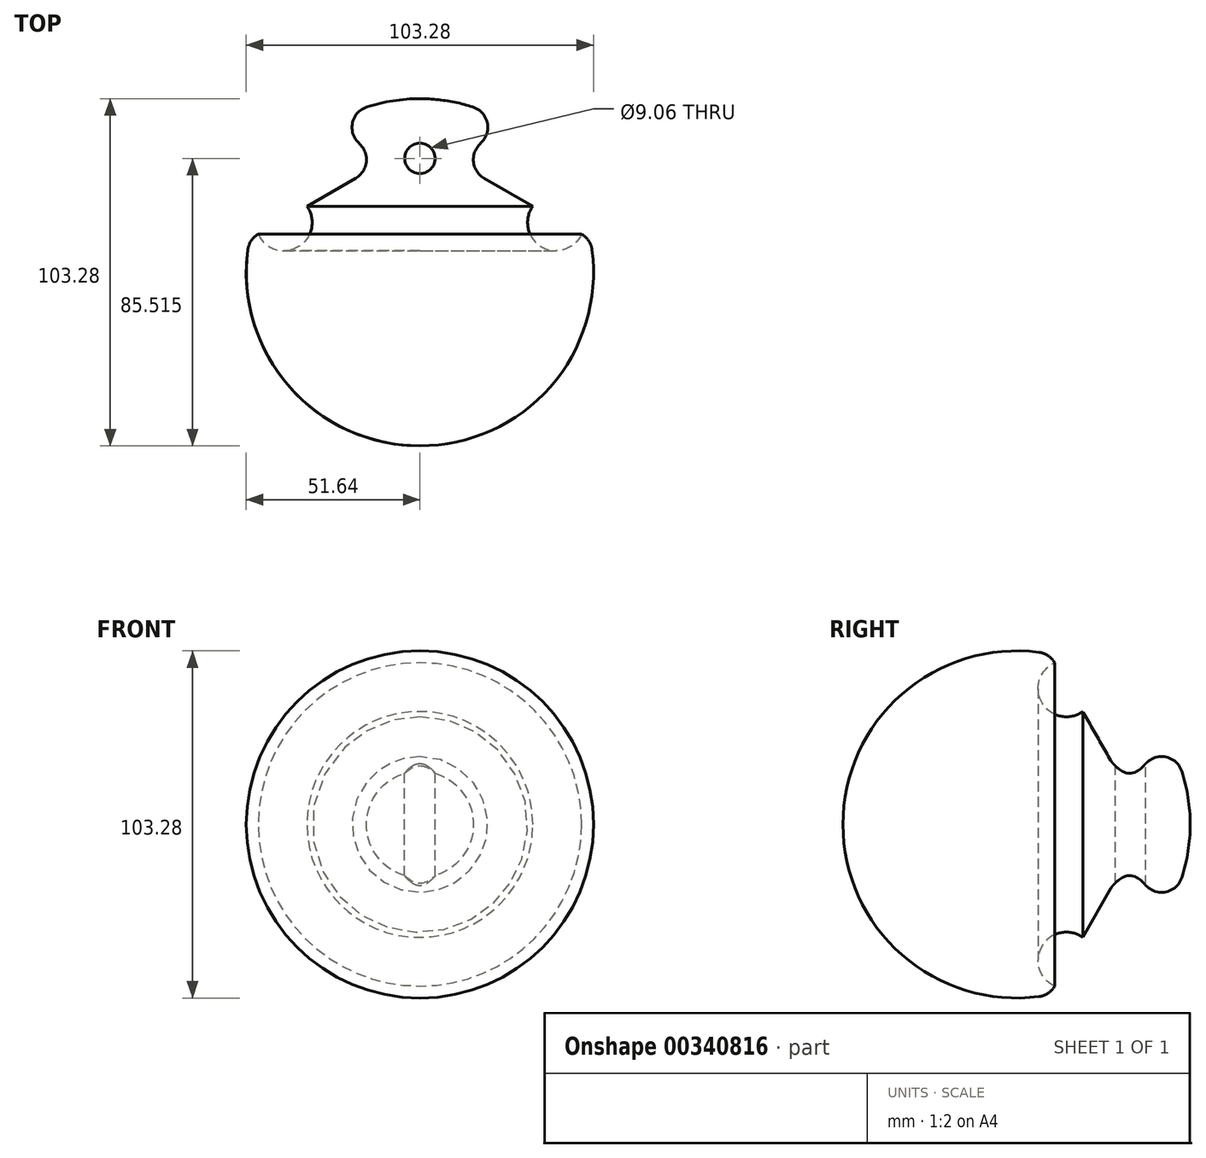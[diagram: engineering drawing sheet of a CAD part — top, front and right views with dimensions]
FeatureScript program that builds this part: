
annotation { "Feature Type Name" : "Feature", "Feature Type Description" : "" }
export const myFeature = defineFeature(function(context is Context, id is Id, definition is map)
    precondition{}
    {
        {
            var Q0;
            Q0=qCreatedBy(makeId("Top.planeOp"),FACE);
            var sketch = newSketch(context, id + "F0", { "sketchPlane" : qUnion([Q0])});
            skArc(sketch, "E0", {"start": v(0, 51.64) * mm, "mid": v(-7.98, 51.02) * mm, "end": v(-15.77, 49.18) * mm});
            skLineSegment(sketch, "E1", {"start": v(0, 51.64) * mm, "end": v(0, -51.64) * mm});
            skLineSegment(sketch, "E2", {"start": v(-18.54, 38.86) * mm, "end": v(-17.56, 37.78) * mm});
            skLineSegment(sketch, "E3", {"start": v(-19.1, 28) * mm, "end": v(-33.59, 19.67) * mm});
            skArc(sketch, "E4.trimOffspring", {"start": v(-51.21, 6.65) * mm, "mid": v(-38.8, -34.09) * mm, "end": v(0, -51.64) * mm});
            skPoint(sketch, "E5.visualSharp", {"position": v(-24.52, 45.46) * mm});
            skArc(sketch, "E5.filletArc", {"start": v(-15.77, 49.18) * mm, "mid": v(-19.97, 44.77) * mm, "end": v(-18.54, 38.86) * mm});
            skPoint(sketch, "E6.visualSharp", {"position": v(-50.7, 9.83) * mm});
            skArc(sketch, "E6.filletArc", {"start": v(-48.08, 11.34) * mm, "mid": v(-50.2, 9.36) * mm, "end": v(-51.21, 6.65) * mm});
            skPoint(sketch, "E7.visualSharp", {"position": v(-12.26, 31.94) * mm});
            skArc(sketch, "E7.filletArc", {"start": v(-19.1, 28) * mm, "mid": v(-15.99, 32.53) * mm, "end": v(-17.56, 37.78) * mm});
            skArc(sketch, "E8", {"start": v(-48.08, 11.34) * mm, "mid": v(-36.25, 7.53) * mm, "end": v(-33.59, 19.67) * mm});
            skSolve(sketch);
        }
        {
            var Q0;
            Q0=makeQuery(id+"F0.imprint","IMPRINT",FACE,{"disambiguationData":[TD([[makeQuery(id+"F0.imprint","IMPRINT",EDGE,{"derivedFrom":sQuery(id+"F0.wireOp",EDGE,"E0")}),1.0]])]});
            var Q1;
            Q1=sQuery(id+"F0.wireOp",EDGE,"E1");
            revolve(context, id + "F1", {"entities" : qUnion([Q0]), "axis" : qUnion([Q1]), "revolveType" : RevolveType.FULL});
        }
        {
            var Q0;
            Q0=qCreatedBy(makeId("Top.planeOp"),FACE);
            var sketch = newSketch(context, id + "F2", { "sketchPlane" : qUnion([Q0])});
            skCircle(sketch, "E9", {"center": v(0, 33.88) * mm, "radius": 4.53 * mm});
            skSolve(sketch);
        }
        {
            var Q0;
            Q0 = qSketchRegion(id + "F2", true);
            extrude(context, id + "F3", {"entities" : qUnion([Q0]), "operationType" : NewBodyOperationType.REMOVE, "oppositeDirection" : true, "depth" : 43.18 * mm});
        }
        {
            var Q0;
            Q0 = qSketchRegion(id + "F2", true);
            extrude(context, id + "F4", {"entities" : qUnion([Q0]), "operationType" : NewBodyOperationType.REMOVE, "depth" : 68.07 * mm});
        }
    });
